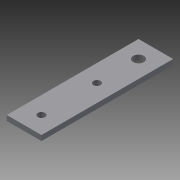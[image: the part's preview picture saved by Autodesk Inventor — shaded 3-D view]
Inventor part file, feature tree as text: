
AUTODESK INVENTOR PART (.ipt)
format: ipt  version: 2015 (Build 190159000, 159)  size: 88,064 bytes
history: native  units: mm
features: sketch x3, hole x2, other x1, extrude x1
ambient origin geometry x8: Origin, YZ Plane, XZ Plane, XY Plane, X Axis, Y Axis, Z Axis, Center Point
bodies: Body1 (feature_tree)
feature tree (7):
  other  "ソリッド1"
  extrude  "押し出し1"  Depth=10.0mm
  hole  "穴1"  [1 undecoded]
  hole  "穴2"  [1 undecoded]
  sketch  "スケッチ1"
  sketch  "スケッチ2"
  sketch  "スケッチ3"
note: 2 required parameter values undecoded (feature->parameter linkage not recoverable at this tier; creation-order binding heuristic only, values carry confidence <= 0.55)
